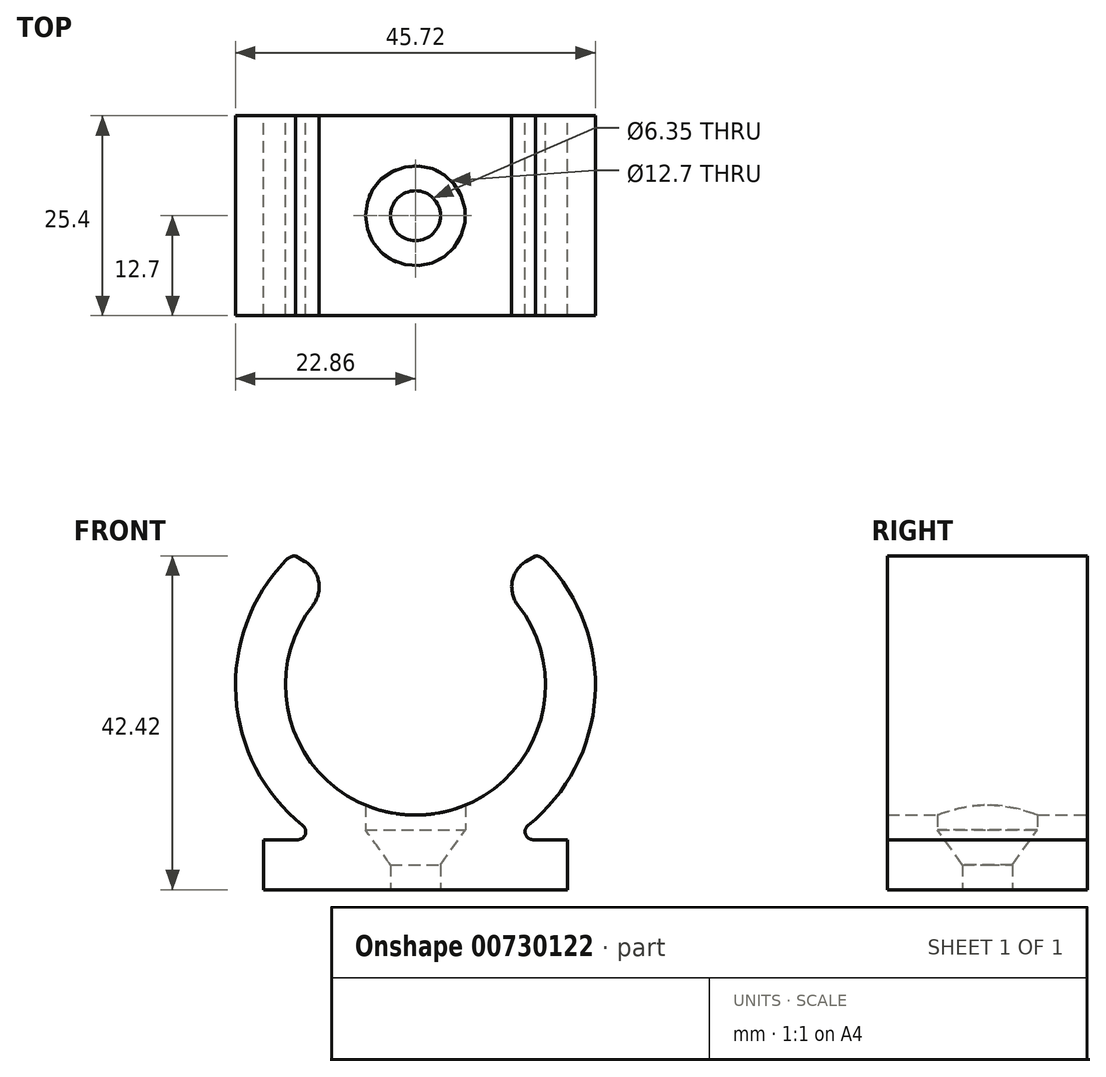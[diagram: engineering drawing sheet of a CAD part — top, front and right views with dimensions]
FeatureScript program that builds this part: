
annotation { "Feature Type Name" : "Feature", "Feature Type Description" : "" }
export const myFeature = defineFeature(function(context is Context, id is Id, definition is map)
    precondition{}
    {
        {
            var Q0;
            Q0=qCreatedBy(makeId("Front.planeOp"),FACE);
            var sketch = newSketch(context, id + "F0", { "sketchPlane" : qUnion([Q0])});
            skPoint(sketch, "E0.middle", {"position": v(0, 0) * mm});
            skArc(sketch, "E1", {"start": v(-15.9, 39.24) * mm, "mid": v(-22.7, 20.17) * mm, "end": v(-11.7, 3.17) * mm});
            skPoint(sketch, "E1.first.point", {"position": v(-20.66, 32.6) * mm});
            skPoint(sketch, "E1.second.point", {"position": v(20.47, 12.64) * mm});
            skPoint(sketch, "E1.third.point", {"position": v(-0.22, -0.05) * mm});
            skLineSegment(sketch, "E2.bottom", {"start": v(15.9, 39.24) * mm, "end": v(1.63, 39.24) * mm});
            skPoint(sketch, "E2.middle", {"position": v(0, 45.67) * mm});
            skArc(sketch, "E3.0", {"start": v(-1.63, 39.24) * mm, "mid": v(0, 6.3) * mm, "end": v(1.63, 39.24) * mm});
            skPoint(sketch, "E2.right.end.orphan", {"position": v(-20.47, 52.1) * mm});
            skPoint(sketch, "E2.left.end.orphan", {"position": v(13.1, 52.1) * mm});
            skPoint(sketch, "E4.orphan", {"position": v(20.47, 39.24) * mm});
            skPoint(sketch, "E5.orphan", {"position": v(-13.1, 39.24) * mm});
            skLineSegment(sketch, "E6.trimOffspring", {"start": v(-1.63, 39.24) * mm, "end": v(-15.9, 39.24) * mm});
            skLineSegment(sketch, "E7.top", {"start": v(19.32, -3.17) * mm, "end": v(-19.32, -3.17) * mm});
            skLineSegment(sketch, "E7.left", {"start": v(19.32, 3.17) * mm, "end": v(19.32, -3.17) * mm});
            skLineSegment(sketch, "E7.right", {"start": v(-19.32, 3.17) * mm, "end": v(-19.32, -3.18) * mm});
            skArc(sketch, "E8.trimOffspring", {"start": v(11.7, 3.18) * mm, "mid": v(22.7, 20.17) * mm, "end": v(15.9, 39.24) * mm});
            skLineSegment(sketch, "E9", {"start": v(19.32, 3.18) * mm, "end": v(11.7, 3.18) * mm});
            skLineSegment(sketch, "E10", {"start": v(-11.7, 3.18) * mm, "end": v(-19.32, 3.18) * mm});
            skSolve(sketch);
        }
        {
            var Q0;
            Q0=makeQuery(id+"F0.imprint","IMPRINT",FACE,{"disambiguationData":[TD([[makeQuery(id+"F0.imprint","IMPRINT",EDGE,{"derivedFrom":sQuery(id+"F0.wireOp",EDGE,"E7.top")}),-1.0]])]});
            extrude(context, id + "F1", {"entities" : qUnion([Q0]), "endBound" : BoundingType.SYMMETRIC, "depth" : 25.4 * mm, "offsetDistance" : 25.4 * mm});
        }
        {
            var Q0;
            {var subQ0=sQuery(id+"F0.wireOp",EDGE,"E1");Q0=makeQuery(id+"F0.imprint","IMPRINT",FACE,{"disambiguationData":[TD([[makeQuery(id+"F0.imprint","IMPRINT",EDGE,{"derivedFrom":subQ0}),1.0]])]});}
            extrude(context, id + "F2", {"entities" : qUnion([Q0]), "operationType" : NewBodyOperationType.ADD, "endBound" : BoundingType.SYMMETRIC, "depth" : 25.4 * mm, "offsetDistance" : 25.4 * mm});
        }
        {
            var Q0;
            {var subQ0=sQuery(id+"F0.wireOp",EDGE,"E2.bottom");Q0=makeQuery(id+"F0.imprint","IMPRINT",FACE,{"disambiguationData":[TD([[makeQuery(id+"F0.imprint","IMPRINT",EDGE,{"derivedFrom":subQ0}),1.0]])]});}
            extrude(context, id + "F3", {"entities" : qUnion([Q0]), "operationType" : NewBodyOperationType.ADD, "endBound" : BoundingType.SYMMETRIC, "depth" : 25.4 * mm, "offsetDistance" : 25.4 * mm});
        }
        {
            var Q0;
            Q0=makeQuery(id+"F2.opExtrude","SWEPT_EDGE",EDGE,{"disambiguationData":[OSD([sQuery(id+"F0.wireOp",EDGE,"E3.0"),sQuery(id+"F0.wireOp",EDGE,"E6.trimOffspring")])]});
            var Q1;
            Q1=makeQuery(id+"F3.opExtrude","SWEPT_EDGE",EDGE,{"disambiguationData":[OSD([sQuery(id+"F0.wireOp",EDGE,"E2.bottom"),sQuery(id+"F0.wireOp",EDGE,"E3.0")])]});
            var Q2;
            Q2=makeQuery(id+"F1.opExtrude","SWEPT_EDGE",EDGE,{"disambiguationData":[OSD([sQuery(id+"F0.wireOp",EDGE,"E3.0"),sQuery(id+"F0.wireOp",EDGE,"E6.trimOffspring")])]});
            var Q3;
            Q3=makeQuery(id+"F1.opExtrude","SWEPT_EDGE",EDGE,{"disambiguationData":[OSD([sQuery(id+"F0.wireOp",EDGE,"E2.bottom"),sQuery(id+"F0.wireOp",EDGE,"E3.0")])]});
            chamfer(context, id + "F4", {"entities" : qUnion([Q0, Q1, Q2, Q3]), "chamferType" : ChamferType.OFFSET_ANGLE, "width" : 50.8 * mm, "oppositeDirection" : false, "angle" : 80 * degree, "tangentPropagation" : true});
        }
        {
            var Q0;
            Q0=qCreatedBy(makeId("Front.planeOp"),FACE);
            var sketch = newSketch(context, id + "F5", { "sketchPlane" : qUnion([Q0])});
            skLineSegment(sketch, "E11", {"start": v(0, 0) * mm, "end": v(0, 12.7) * mm});
            skLineSegment(sketch, "E12", {"start": v(0, 12.7) * mm, "end": v(6.35, 12.7) * mm});
            skLineSegment(sketch, "E13", {"start": v(6.35, 12.7) * mm, "end": v(6.35, 4.44) * mm});
            skLineSegment(sketch, "E14", {"start": v(0, 0) * mm, "end": v(0, -4.45) * mm});
            skLineSegment(sketch, "E15", {"start": v(0, -4.45) * mm, "end": v(3.18, -4.45) * mm});
            skLineSegment(sketch, "E16", {"start": v(3.18, -4.45) * mm, "end": v(3.18, 0) * mm});
            skLineSegment(sketch, "E17", {"start": v(3.18, 0) * mm, "end": v(6.35, 4.44) * mm});
            skSolve(sketch);
        }
        {
            var Q0;
            Q0=makeQuery(id+"F5.imprint","IMPRINT",FACE,{"disambiguationData":[TD([[makeQuery(id+"F5.imprint","IMPRINT",EDGE,{"derivedFrom":sQuery(id+"F5.wireOp",EDGE,"E11")}),-1.0]])]});
            var Q1;
            Q1=sQuery(id+"F5.wireOp",EDGE,"E11");
            revolve(context, id + "F6", {"surfaceOperationType" : NewSurfaceOperationType.NEW, "entities" : qUnion([Q0]), "axis" : qUnion([Q1]), "revolveType" : RevolveType.FULL});
        }
        {
            var Q0;
            Q0=makeQuery(id+"F6.opRevolve","SWEPT_BODY",BODY,{"disambiguationData":[OSD([sQuery(id+"F5.wireOp",EDGE,"E11"),sQuery(id+"F5.wireOp",EDGE,"E12"),sQuery(id+"F5.wireOp",EDGE,"E13"),sQuery(id+"F5.wireOp",EDGE,"E14"),sQuery(id+"F5.wireOp",EDGE,"E15"),sQuery(id+"F5.wireOp",EDGE,"E16"),sQuery(id+"F5.wireOp",EDGE,"E17")])]});
            var Q1;
            Q1=makeQuery(id+"F1.opExtrude","SWEPT_BODY",BODY,{"disambiguationData":[OSD([sQuery(id+"F0.wireOp",EDGE,"E7.top"),sQuery(id+"F0.wireOp",EDGE,"E7.left"),sQuery(id+"F0.wireOp",EDGE,"E7.right"),sQuery(id+"F0.wireOp",EDGE,"qXzntEkX-schh-RJY0-iEMT-iMVs1TcgXbfG")])]});
            booleanBodies(context, id + "F7", {"operationType" : BooleanOperationType.SUBTRACTION, "tools" : qUnion([Q0]), "targets" : qUnion([Q1])});
        }
        {
            var Q0;
            {var subQ0=sQuery(id+"F0.wireOp",EDGE,"E6.trimOffspring");Q0=makeQuery(id+"F6TPtiZcX2O7DIu_1.opChamfer","BLEND_EDGE",EDGE,{"blendedFrom":[makeQuery(id+"F1.opExtrude","SWEPT_EDGE",EDGE,{"disambiguationData":[OSD([sQuery(id+"F0.wireOp",EDGE,"E3.0"),subQ0])]}),makeQuery(id+"F1.opExtrude","SWEPT_FACE",FACE,{"disambiguationData":[OSD([subQ0])]})],"blendedInto":[makeQuery(id+"F1.opExtrude","SWEPT_FACE",FACE,{"disambiguationData":[OSD([subQ0])]})]});}
            var Q1;
            Q1=makeQuery(id+"F1.opExtrude","SWEPT_EDGE",EDGE,{"disambiguationData":[OSD([sQuery(id+"F0.wireOp",EDGE,"E1"),sQuery(id+"F0.wireOp",EDGE,"E6.trimOffspring")])]});
            var Q2;
            Q2=makeQuery(id+"F1.opExtrude","SWEPT_EDGE",EDGE,{"disambiguationData":[OSD([sQuery(id+"F0.wireOp",EDGE,"E2.bottom"),sQuery(id+"F0.wireOp",EDGE,"E8.trimOffspring")])]});
            var Q3;
            {var subQ0=sQuery(id+"F0.wireOp",EDGE,"E2.bottom");Q3=makeQuery(id+"F6TPtiZcX2O7DIu_1.opChamfer","BLEND_EDGE",EDGE,{"blendedFrom":[makeQuery(id+"F1.opExtrude","SWEPT_EDGE",EDGE,{"disambiguationData":[OSD([subQ0,sQuery(id+"F0.wireOp",EDGE,"E3.0")])]}),makeQuery(id+"F1.opExtrude","SWEPT_FACE",FACE,{"disambiguationData":[OSD([subQ0])]})],"blendedInto":[makeQuery(id+"F1.opExtrude","SWEPT_FACE",FACE,{"disambiguationData":[OSD([subQ0])]})]});}
            var Q4;
            {var subQ0=sQuery(id+"F0.wireOp",EDGE,"E3.0");Q4=makeQuery(id+"F6TPtiZcX2O7DIu_1.opChamfer","BLEND_EDGE",EDGE,{"blendedFrom":[makeQuery(id+"F1.opExtrude","SWEPT_EDGE",EDGE,{"disambiguationData":[OSD([subQ0,sQuery(id+"F0.wireOp",EDGE,"E6.trimOffspring")])]}),makeQuery(id+"F1.opExtrude","SWEPT_FACE",FACE,{"disambiguationData":[OSD([subQ0])]})],"blendedInto":[makeQuery(id+"F1.opExtrude","SWEPT_FACE",FACE,{"disambiguationData":[OSD([subQ0])]})]});}
            var Q5;
            {var subQ0=sQuery(id+"F0.wireOp",EDGE,"E3.0");Q5=makeQuery(id+"F6TPtiZcX2O7DIu_1.opChamfer","BLEND_EDGE",EDGE,{"blendedFrom":[makeQuery(id+"F1.opExtrude","SWEPT_EDGE",EDGE,{"disambiguationData":[OSD([sQuery(id+"F0.wireOp",EDGE,"E2.bottom"),subQ0])]}),makeQuery(id+"F1.opExtrude","SWEPT_FACE",FACE,{"disambiguationData":[OSD([subQ0])]})],"blendedInto":[makeQuery(id+"F1.opExtrude","SWEPT_FACE",FACE,{"disambiguationData":[OSD([subQ0])]})]});}
            fillet(context, id + "F8", {"entities" : qUnion([Q0, Q1, Q2, Q3, Q4, Q5]), "radius" : 1.9 * mm, "tangentPropagation" : true, "allowEdgeOverflow" : false});
        }
        {
            var Q0;
            {var subQ0=sQuery(id+"F0.wireOp",EDGE,"E3.0");Q0=makeQuery(id+"F4.opChamfer","BLEND_EDGE",EDGE,{"blendedFrom":[makeQuery(id+"F1.opExtrude","SWEPT_EDGE",EDGE,{"disambiguationData":[OSD([sQuery(id+"F0.wireOp",EDGE,"E2.bottom"),subQ0])]}),makeQuery(id+"F1.opExtrude","SWEPT_FACE",FACE,{"disambiguationData":[OSD([subQ0])]})],"blendedInto":[makeQuery(id+"F1.opExtrude","SWEPT_FACE",FACE,{"disambiguationData":[OSD([subQ0])]})]});}
            var Q1;
            {var subQ0=sQuery(id+"F0.wireOp",EDGE,"E3.0");Q1=makeQuery(id+"F4.opChamfer","BLEND_EDGE",EDGE,{"blendedFrom":[makeQuery(id+"F1.opExtrude","SWEPT_EDGE",EDGE,{"disambiguationData":[OSD([subQ0,sQuery(id+"F0.wireOp",EDGE,"E6.trimOffspring")])]}),makeQuery(id+"F1.opExtrude","SWEPT_FACE",FACE,{"disambiguationData":[OSD([subQ0])]})],"blendedInto":[makeQuery(id+"F1.opExtrude","SWEPT_FACE",FACE,{"disambiguationData":[OSD([subQ0])]})]});}
            fillet(context, id + "F9", {"entities" : qUnion([Q0, Q1]), "radius" : 3.8 * mm, "tangentPropagation" : true, "allowEdgeOverflow" : false});
        }
        {
            var Q0;
            Q0=makeQuery(id+"F1.opExtrude","SWEPT_EDGE",EDGE,{"disambiguationData":[OSD([sQuery(id+"F0.wireOp",EDGE,"E8.trimOffspring"),sQuery(id+"F0.wireOp",EDGE,"E9")])]});
            var Q1;
            Q1=makeQuery(id+"F1.opExtrude","SWEPT_EDGE",EDGE,{"disambiguationData":[OSD([sQuery(id+"F0.wireOp",EDGE,"E1"),sQuery(id+"F0.wireOp",EDGE,"E10")])]});
            fillet(context, id + "F10", {"entities" : qUnion([Q0, Q1]), "radius" : 1.02 * mm, "tangentPropagation" : true, "allowEdgeOverflow" : false});
        }
    });
